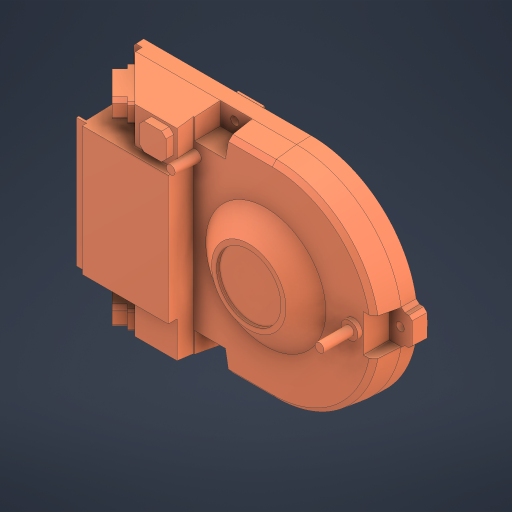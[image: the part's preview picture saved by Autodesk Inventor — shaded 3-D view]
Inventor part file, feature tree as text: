
AUTODESK INVENTOR PART (.ipt)
format: ipt  version: 2024 (Build 280153000, 153)  size: 357,888 bytes
history: native  units: in
note: dims shown in document units (in); Inventor stores cm internally (conversion verified against a paired STEP export)
features: other x2, extrude x1, sketch x1
ambient origin geometry x8: Origin, YZ Plane, XZ Plane, XY Plane, X Axis, Y Axis, Z Axis, Center Point
bodies: Body1 (feature_tree)
feature tree (4):
  other  "Sólido1"
  extrude  "Extrusión1"  Depth=1.9685in
  sketch  "Boceto1"  dims[d0=14.7638in d1=17.0477in d2=0.7283in d3=0.3937in d4=1.9685in d5=0.0in]
  parser-record x1  (decoder bookkeeping rows leaked as tree rows — omitted from the tree; the rows remain in map.json)
